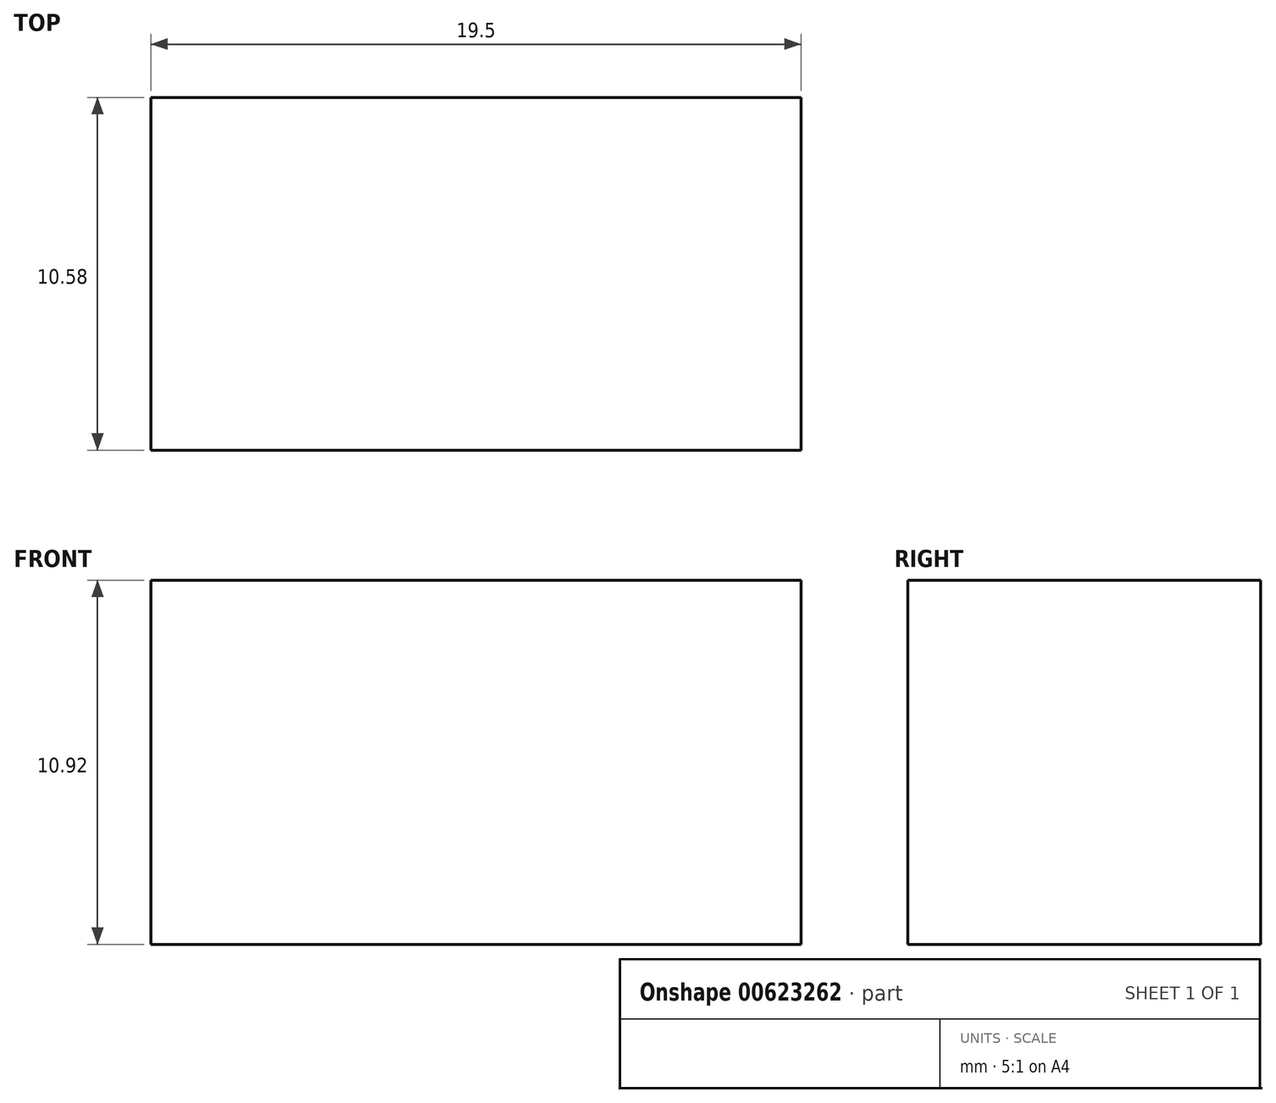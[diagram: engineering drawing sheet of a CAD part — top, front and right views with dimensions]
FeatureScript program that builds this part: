
annotation { "Feature Type Name" : "Feature", "Feature Type Description" : "" }
export const myFeature = defineFeature(function(context is Context, id is Id, definition is map)
    precondition{}
    {
        {
            var Q0;
            Q0=qCreatedBy(makeId("Top.planeOp"),FACE);
            var sketch = newSketch(context, id + "F0", { "sketchPlane" : qUnion([Q0])});
            skLineSegment(sketch, "E0.bottom", {"start": v(9.75, -5.29) * mm, "end": v(-9.75, -5.29) * mm});
            skLineSegment(sketch, "E0.top", {"start": v(9.75, 5.29) * mm, "end": v(-9.75, 5.29) * mm});
            skLineSegment(sketch, "E0.left", {"start": v(9.75, -5.29) * mm, "end": v(9.75, 5.29) * mm});
            skLineSegment(sketch, "E0.right", {"start": v(-9.75, -5.29) * mm, "end": v(-9.75, 5.29) * mm});
            skPoint(sketch, "E0.middle", {"position": v(0, 0) * mm});
            skSolve(sketch);
        }
        {
            var Q0;
            Q0 = qSketchRegion(id + "F0", true);
            extrude(context, id + "F1", {"entities" : qUnion([Q0]), "depth" : 10.92 * mm, "offsetDistance" : 25.4 * mm});
        }
    });
